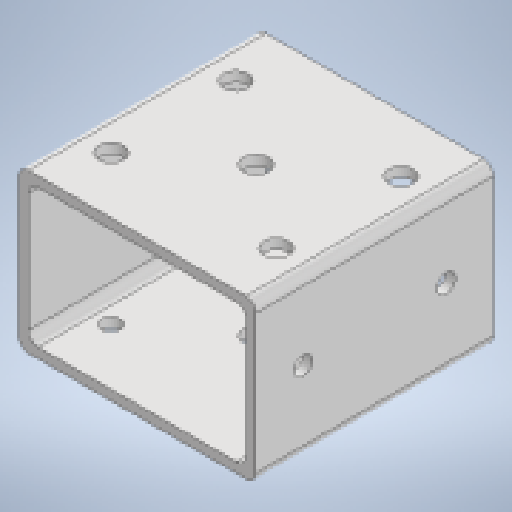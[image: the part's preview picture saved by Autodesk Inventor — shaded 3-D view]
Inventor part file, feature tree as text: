
AUTODESK INVENTOR PART (.ipt)
format: ipt  version: 2023 (Build 270158000, 158)  size: 262,144 bytes
history: native  units: in
note: dims shown in document units (in); Inventor stores cm internally (conversion verified against a paired STEP export)
features: extrude x5, sketch x5, shell x1, fillet x1, projected_geometry x1
ambient origin geometry x8: Origin, YZ Plane, XZ Plane, XY Plane, X Axis, Y Axis, Z Axis, Center Point
bodies: Solid1 (feature_tree)
feature tree (13):
  extrude  "Extrusion1"  Depth=2.0in
  shell  "Shell1"  Thickness=3.0in
  extrude  "Extrusion2"  Depth=0.125in
  extrude  "Extrusion3"  Depth=1.5748in
  fillet  "Fillet1"  Radius=4.0in
  extrude  "Extrusion4"  Depth=4.0in TaperAngle=0.0deg
  extrude  "Extrusion5"  Depth=3.0in
  sketch  "Sketch1"  dims[d0=3.0in d1=2.0in d2=3.0in d3=0.0in]
  sketch  "Sketch2"  dims[d4=0.125in d5=0.2362in]
  sketch  "Sketch3"  dims[d6=2.0866in d7=1.5748in d8=4.0in d9=0.0in]
  sketch  "Sketch4"  dims[d10=0.315in d11=4.0in d12=0.0in]
  sketch  "Sketch5"  dims[d13=0.125in d14=0.315in d15=3.0in d16=0.0in d17=0.2362in d18=1.811in d19=1.0in d20=0.0in]
  projected_geometry  "Projected Loop1"
